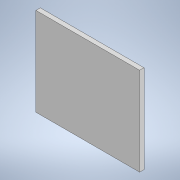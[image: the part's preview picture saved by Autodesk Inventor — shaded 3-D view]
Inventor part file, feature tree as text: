
AUTODESK INVENTOR PART (.ipt)
format: ipt  version: 2020 (Build 240168000, 168)  size: 92,672 bytes
history: native  units: mm
features: extrude x1, sketch x1
ambient origin geometry x8: Origin, YZ Plane, XZ Plane, XY Plane, X Axis, Y Axis, Z Axis, Center Point
bodies: Solid1 (feature_tree)
feature tree (2):
  extrude  "Extrusion1"  Depth=47.0mm
  sketch  "Sketch1"  dims[d0=2.0mm d1=47.0mm d2=40.0mm d3=0.0mm]
